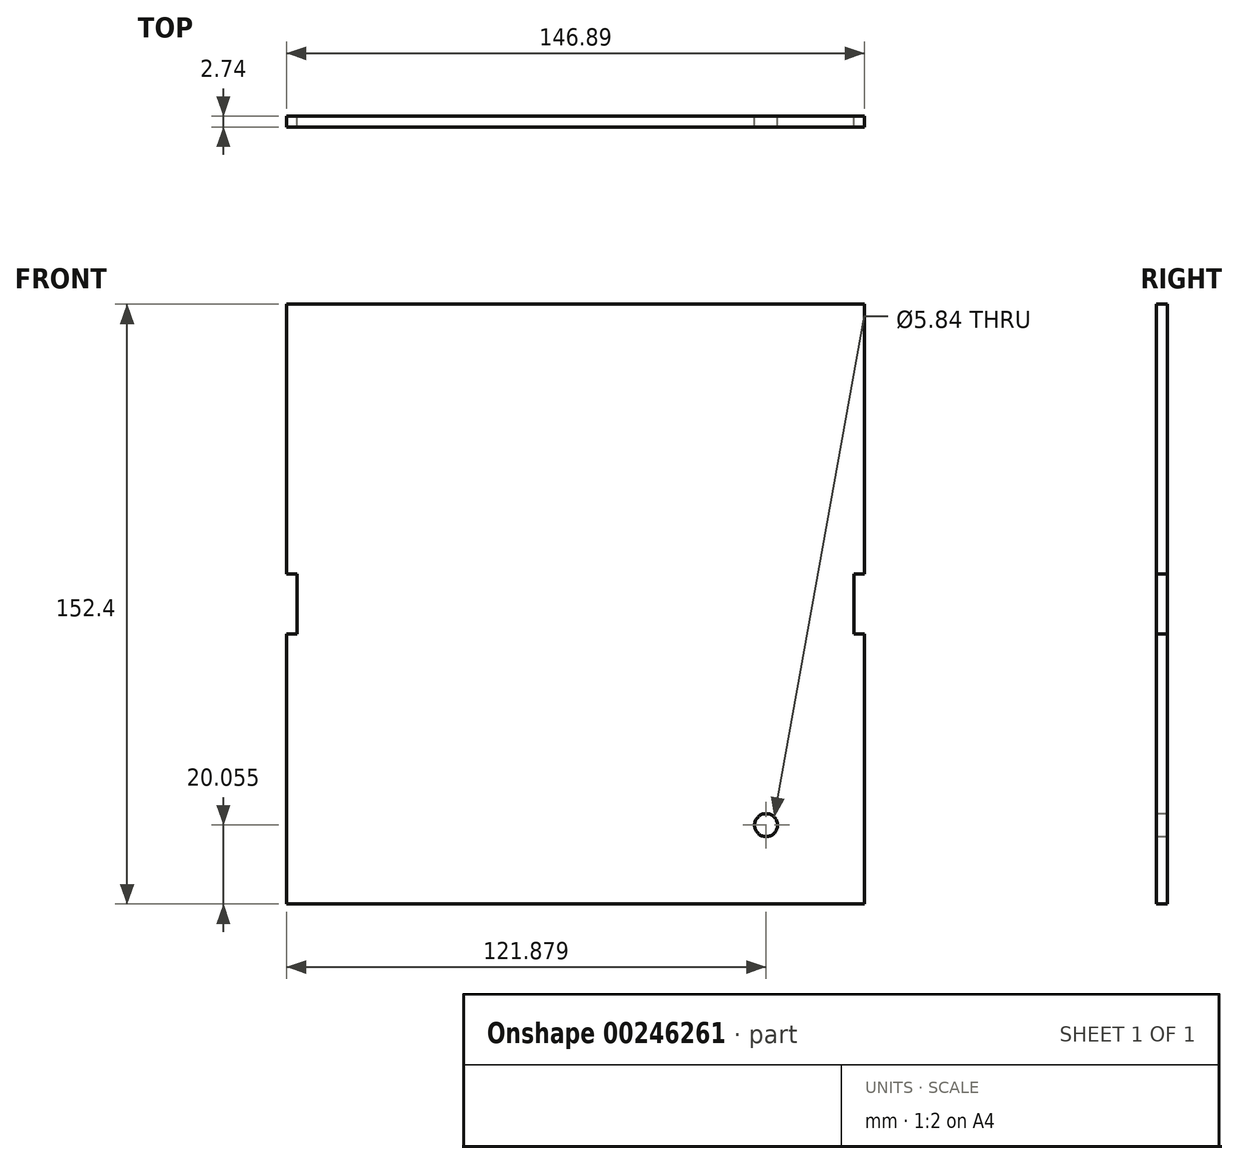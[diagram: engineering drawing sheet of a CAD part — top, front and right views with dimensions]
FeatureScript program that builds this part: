
annotation { "Feature Type Name" : "Feature", "Feature Type Description" : "" }
export const myFeature = defineFeature(function(context is Context, id is Id, definition is map)
    precondition{}
    {
        {
            var Q0;
            Q0=qCreatedBy(makeId("Front.planeOp"),FACE);
            var sketch = newSketch(context, id + "F0", { "sketchPlane" : qUnion([Q0])});
            skLineSegment(sketch, "E0.bottom", {"start": v(-81.08, 118.1) * mm, "end": v(65.81, 118.1) * mm});
            skLineSegment(sketch, "E0.top", {"start": v(-81.08, -34.3) * mm, "end": v(65.81, -34.3) * mm});
            skLineSegment(sketch, "E0.left", {"start": v(-81.08, 118.1) * mm, "end": v(-81.08, -34.3) * mm});
            skLineSegment(sketch, "E0.right", {"start": v(65.81, 118.1) * mm, "end": v(65.81, -34.3) * mm});
            skLineSegment(sketch, "E1", {"start": v(0, 120.84) * mm, "end": v(0, 118.1) * mm});
            skLineSegment(sketch, "E2.MirrorCS", {"start": v(-15.24, 120.84) * mm, "end": v(-15.24, 118.1) * mm});
            skLineSegment(sketch, "E3.MirrorCS", {"start": v(-7.62, -37.05) * mm, "end": v(-15.24, -37.05) * mm});
            skLineSegment(sketch, "E4.MirrorCS", {"start": v(-15.24, -37.05) * mm, "end": v(-15.24, -34.3) * mm});
            skLineSegment(sketch, "E5.MirrorCS", {"start": v(-7.62, -37.05) * mm, "end": v(0, -37.05) * mm});
            skLineSegment(sketch, "E6.MirrorCS", {"start": v(0, -37.05) * mm, "end": v(0, -34.3) * mm});
            skLineSegment(sketch, "E7", {"start": v(-78.33, 49.52) * mm, "end": v(-81.08, 49.52) * mm});
            skLineSegment(sketch, "E8", {"start": v(-15.24, 120.84) * mm, "end": v(0, 120.84) * mm});
            skLineSegment(sketch, "E9.MirrorCS", {"start": v(-78.33, 34.28) * mm, "end": v(-81.08, 34.28) * mm});
            skLineSegment(sketch, "E10", {"start": v(-78.33, 49.52) * mm, "end": v(-78.33, 34.28) * mm});
            skLineSegment(sketch, "E11", {"start": v(-7.63, 118.1) * mm, "end": v(-7.63, -34.3) * mm, "construction": true});
            skLineSegment(sketch, "E12.MirrorCS", {"start": v(63.07, 49.52) * mm, "end": v(65.81, 49.52) * mm});
            skLineSegment(sketch, "E13.MirrorCS", {"start": v(63.07, 49.52) * mm, "end": v(63.07, 34.28) * mm});
            skLineSegment(sketch, "E14.MirrorCS", {"start": v(63.07, 34.28) * mm, "end": v(65.81, 34.28) * mm});
            skCircle(sketch, "E15", {"center": v(40.8, -14.25) * mm, "radius": 2.92 * mm});
            skSolve(sketch);
        }
        {
            var Q0;
            {var subQ0=sQuery(id+"F0.wireOp",EDGE,"E0.left");Q0=makeQuery(id+"F0.imprint","IMPRINT",FACE,{"disambiguationData":[TD([[makeQuery(id+"F0.imprint","IMPRINT",EDGE,{"derivedFrom":subQ0}),1.0]])]});}
            var Q1;
            Q1=makeQuery(id+"F0.imprint","IMPRINT",FACE,{"disambiguationData":[TD([[makeQuery(id+"F0.imprint","IMPRINT",EDGE,{"derivedFrom":sQuery(id+"F0.wireOp",EDGE,"Afd0L3Ea-njuU-8vJm-DEHg-CMs5uG4HDwlt")}),-1.0]])]});
            extrude(context, id + "F1", {"entities" : qUnion([Q0, Q1]), "depth" : 2.74 * mm});
        }
    });
